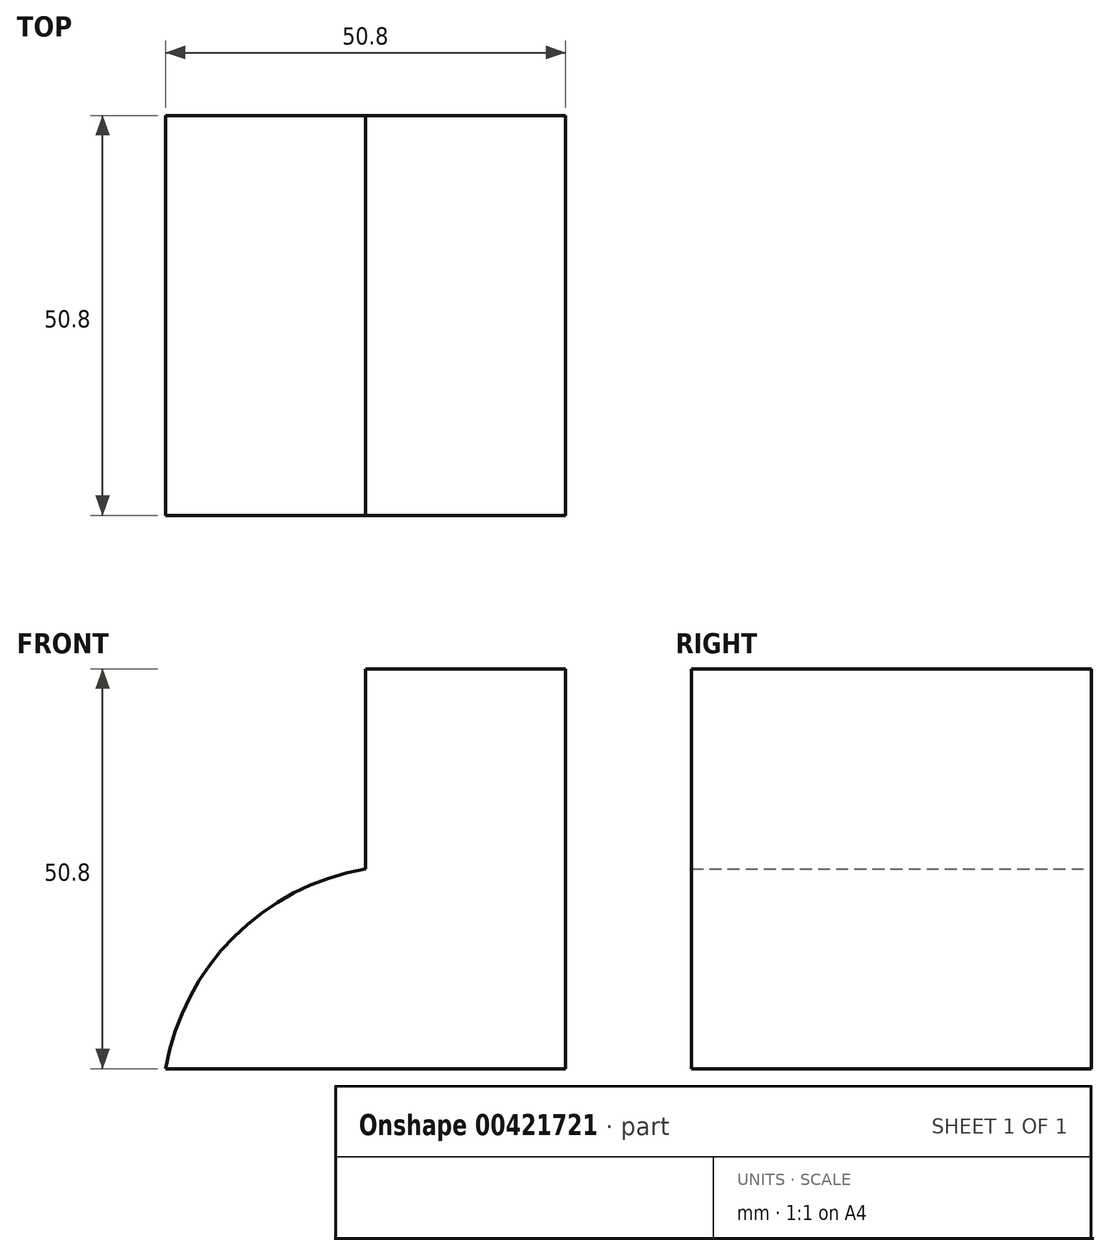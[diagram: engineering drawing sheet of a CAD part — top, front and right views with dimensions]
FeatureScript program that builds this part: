
annotation { "Feature Type Name" : "Feature", "Feature Type Description" : "" }
export const myFeature = defineFeature(function(context is Context, id is Id, definition is map)
    precondition{}
    {
        {
            var Q0;
            Q0=qCreatedBy(makeId("Front.planeOp"),FACE);
            var sketch = newSketch(context, id + "F0", { "sketchPlane" : qUnion([Q0])});
            skLineSegment(sketch, "E0", {"start": v(0, 0) * mm, "end": v(0, 50.8) * mm});
            skLineSegment(sketch, "E1", {"start": v(0, 50.8) * mm, "end": v(-25.4, 50.8) * mm});
            skLineSegment(sketch, "E2", {"start": v(-25.4, 50.8) * mm, "end": v(-25.4, 25.4) * mm});
            skLineSegment(sketch, "E3", {"start": v(0, 0) * mm, "end": v(-50.8, 0) * mm});
            skArc(sketch, "E4", {"start": v(-25.4, 25.4) * mm, "mid": v(-42.12, 16.72) * mm, "end": v(-50.8, 0) * mm});
            skSolve(sketch);
        }
        {
            var Q0;
            Q0=makeQuery(id+"F0.imprint","IMPRINT",FACE,{"disambiguationData":[TD([[makeQuery(id+"F0.imprint","IMPRINT",EDGE,{"derivedFrom":sQuery(id+"F0.wireOp",EDGE,"E0")}),1.0]])]});
            extrude(context, id + "F1", {"entities" : qUnion([Q0]), "depth" : 50.8 * mm});
        }
    });
